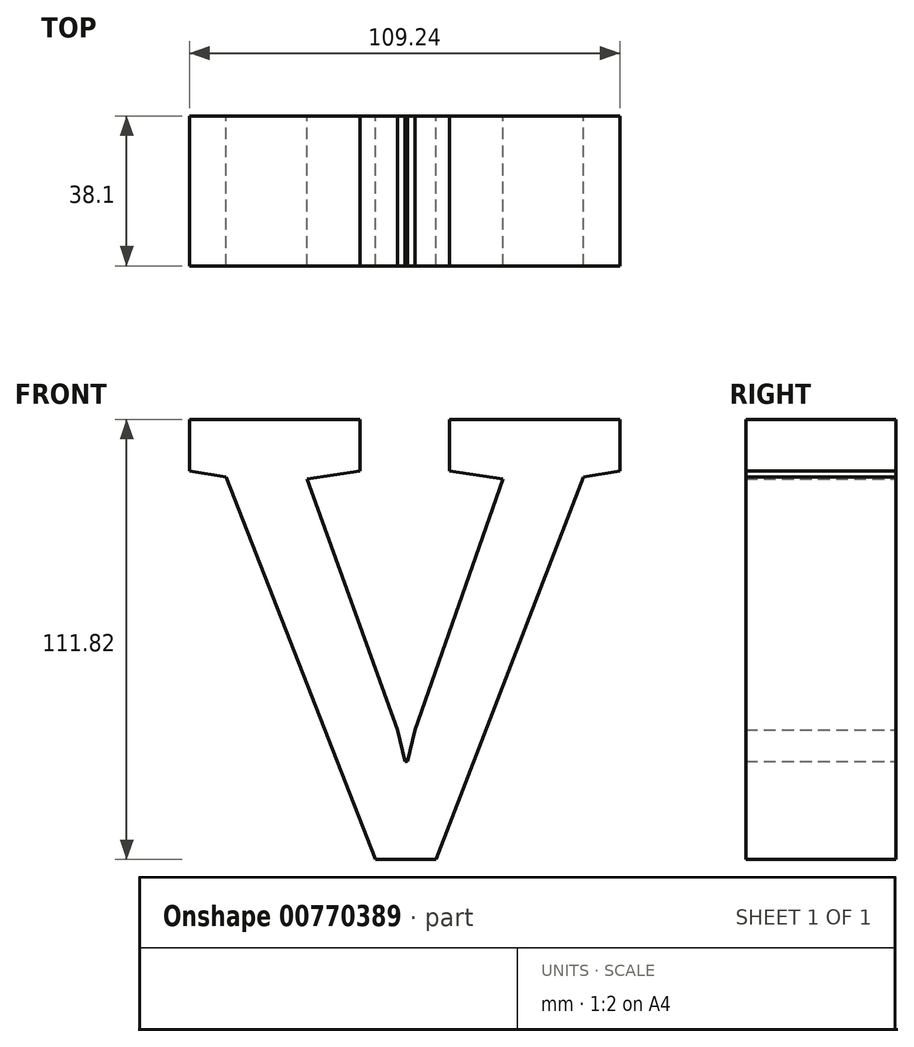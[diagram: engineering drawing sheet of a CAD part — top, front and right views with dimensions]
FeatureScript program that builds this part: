
annotation { "Feature Type Name" : "Feature", "Feature Type Description" : "" }
export const myFeature = defineFeature(function(context is Context, id is Id, definition is map)
    precondition{}
    {
        {
            var Q0;
            Q0=qCreatedBy(makeId("Front.planeOp"),FACE);
            var sketch = newSketch(context, id + "F0", { "sketchPlane" : qUnion([Q0])});
            skText(sketch, "E0", { "text": "v", "fontName": "RobotoSlab-Regular.ttf"});
            const initialGuessF0  = {"E0": [-0.0765, -0.08404, 1, 0, 0.1524]};
            skSetInitialGuess(sketch, initialGuessF0);
            skSolve(sketch);
        }
        {
            var Q0;
            Q0=makeQuery(id+"F0.imprint","IMPRINT",FACE,{"disambiguationData":[TD([[makeQuery(id+"F0.imprint","IMPRINT",EDGE,{"derivedFrom":sQuery(id+"F0.wireOp",EDGE,"E0.sketch_text.stroke-0")}),-1.0]])]});
            extrude(context, id + "F1", {"entities" : qUnion([Q0]), "depth" : 38.1 * mm, "offsetDistance" : 25.4 * mm});
        }
    });
